# Revit family: Haworth_LC6_Table
name_source: partatom
category: Furniture
revit_build: Autodesk Revit 2018 (Build: 20170223_1515(x64)
units: mm (PartAtom-declared; Revit-internal decimal feet)

## family parameters
Always vertical = Yes
Cut with Voids When Loaded = No
OmniClass Number = 23.40.70.14.64.21
OmniClass Title = Systems Furniture
Room Calculation Point = No
Shared = No
Work Plane-Based = No

## types (2) — shared parameters
Actual Depth = 33 1/2"
Actual Height = 28 1/2"
Actual Width = 88 1/2"
Assembly Code = E2020200
Description = Haworth LC6 Table
Glide Finish = Haworth _ Paint _ Collection Black
Manufacturer = Haworth
Model = HCCS-LC6
Revision Number = 4
Size = Verify Final Dim. w/ Haworth
Support Elipse Center = 4 15/16"
Support Height = 23"
Support Location Offset = 5 3/4"
Support Location_Front_Back = 5 93/128"
Support Location_Side = 13"
Table Top Thickness = 9/16"
URL = http://www.haworth.com
URL - Product = https://www.haworth.com
Warranty = http://www.haworth.com

## type names (no varying parameters)
- HCCS-LC6 - Glass Top
- HCCS-LC6 - Wood Top

## geometry (parser evidence)
native form markers: Sweep x2
no freeform markers — native parametric forms only
